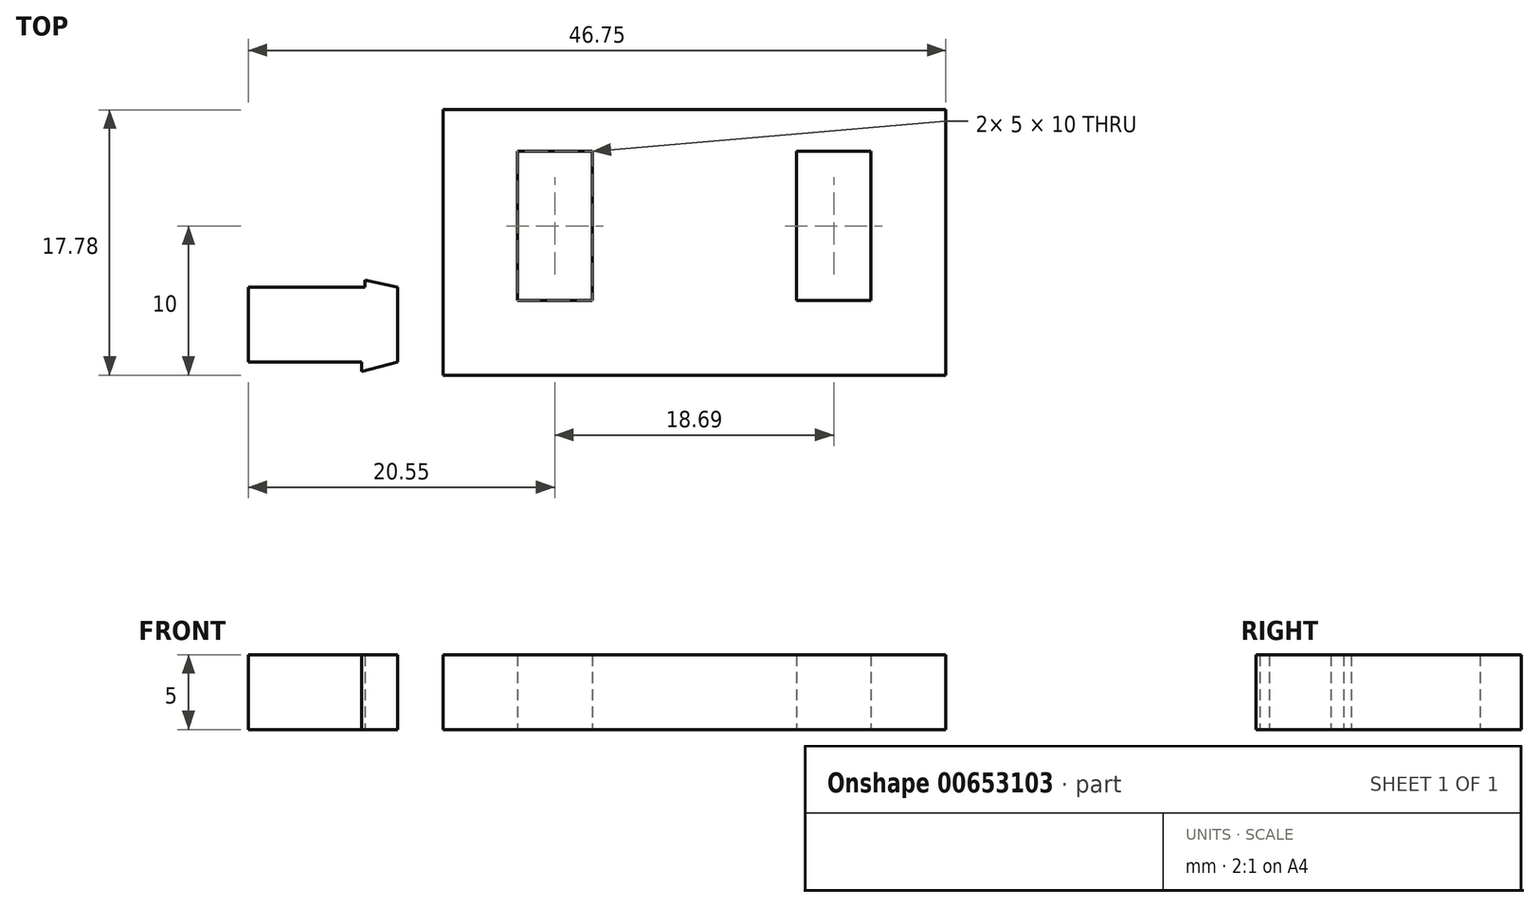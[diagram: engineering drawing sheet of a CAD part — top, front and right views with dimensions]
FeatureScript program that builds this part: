
annotation { "Feature Type Name" : "Feature", "Feature Type Description" : "" }
export const myFeature = defineFeature(function(context is Context, id is Id, definition is map)
    precondition{}
    {
        {
            var Q0;
            Q0=qCreatedBy(makeId("Top.planeOp"),FACE);
            var sketch = newSketch(context, id + "F0", { "sketchPlane" : qUnion([Q0])});
            skLineSegment(sketch, "E0.bottom", {"start": v(16.85, 0) * mm, "end": v(-16.85, 0) * mm});
            skLineSegment(sketch, "E0.left", {"start": v(16.85, 0) * mm, "end": v(16.85, 17.78) * mm});
            skLineSegment(sketch, "E0.right", {"start": v(-16.85, 0) * mm, "end": v(-16.85, 17.78) * mm});
            skPoint(sketch, "E0.middle", {"position": v(0, 0) * mm});
            skLineSegment(sketch, "E1.bottom", {"start": v(-11.85, 5) * mm, "end": v(-6.85, 5) * mm});
            skLineSegment(sketch, "E1.top", {"start": v(-11.85, 15) * mm, "end": v(-6.85, 15) * mm});
            skLineSegment(sketch, "E1.left", {"start": v(-11.85, 5) * mm, "end": v(-11.85, 15) * mm});
            skLineSegment(sketch, "E1.right", {"start": v(-6.85, 5) * mm, "end": v(-6.85, 15) * mm});
            skPoint(sketch, "E2.orphan", {"position": v(-16.85, 10) * mm});
            skPoint(sketch, "E3.end.orphan", {"position": v(-11.85, 10) * mm});
            skPoint(sketch, "E4.startSnap0", {"position": v(-6.85, 10) * mm});
            skLineSegment(sketch, "E5.bottom", {"start": v(6.84, 5) * mm, "end": v(11.84, 5) * mm});
            skLineSegment(sketch, "E5.top", {"start": v(6.84, 15) * mm, "end": v(11.84, 15) * mm});
            skLineSegment(sketch, "E5.left", {"start": v(6.84, 5) * mm, "end": v(6.84, 15) * mm});
            skLineSegment(sketch, "E5.right", {"start": v(11.84, 5) * mm, "end": v(11.84, 15) * mm});
            skPoint(sketch, "E6.end.orphan", {"position": v(6.84, 10) * mm});
            skPoint(sketch, "E7.startSnap0", {"position": v(11.84, 10) * mm});
            skLineSegment(sketch, "E8", {"start": v(-16.85, 17.78) * mm, "end": v(16.85, 17.78) * mm});
            skPoint(sketch, "E0.top.end.orphan", {"position": v(-16.85, 40) * mm});
            skPoint(sketch, "E9.orphan", {"position": v(16.85, 40) * mm});
            skSolve(sketch);
        }
        {
            var Q0;
            Q0 = qSketchRegion(id + "F0", true);
            extrude(context, id + "F1", {"entities" : qUnion([Q0]), "depth" : 5 * mm, "offsetDistance" : 25 * mm});
        }
        {
            var Q0;
            Q0=qCreatedBy(makeId("Top.planeOp"),FACE);
            var sketch = newSketch(context, id + "F2", { "sketchPlane" : qUnion([Q0])});
            skLineSegment(sketch, "E10.bottom", {"start": v(-22.31, 0.88) * mm, "end": v(-29.9, 0.88) * mm});
            skLineSegment(sketch, "E10.top", {"start": v(-22.07, 5.88) * mm, "end": v(-29.9, 5.88) * mm});
            skLineSegment(sketch, "E10.left", {"start": v(-19.9, 0.88) * mm, "end": v(-19.9, 5.88) * mm});
            skLineSegment(sketch, "E10.right", {"start": v(-29.9, 0.88) * mm, "end": v(-29.9, 5.88) * mm});
            skPoint(sketch, "E10.middle", {"position": v(-24.9, 3.38) * mm});
            skLineSegment(sketch, "E11", {"start": v(-19.9, 5.88) * mm, "end": v(-22.07, 6.38) * mm});
            skLineSegment(sketch, "E12", {"start": v(-22.07, 6.38) * mm, "end": v(-22.07, 5.88) * mm});
            skLineSegment(sketch, "E13", {"start": v(-19.9, 0.88) * mm, "end": v(-22.31, 0.24) * mm});
            skLineSegment(sketch, "E14", {"start": v(-22.31, 0.24) * mm, "end": v(-22.31, 0.88) * mm});
            skSolve(sketch);
        }
        {
            var Q0;
            Q0 = qSketchRegion(id + "F2", true);
            extrude(context, id + "F3", {"entities" : qUnion([Q0]), "depth" : 5 * mm, "offsetDistance" : 25 * mm});
        }
    });
